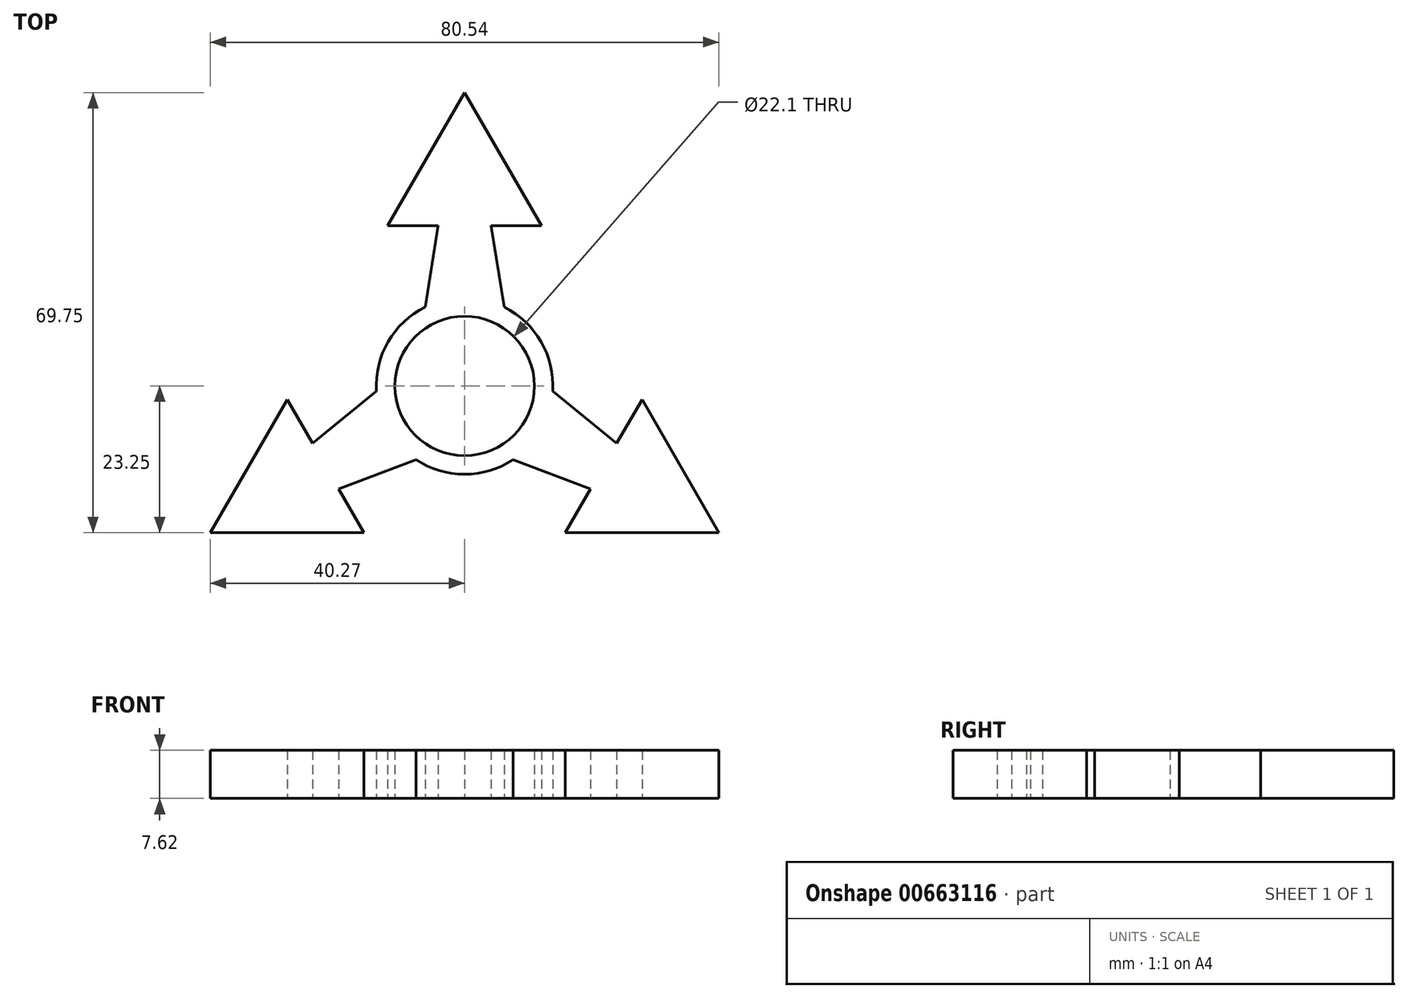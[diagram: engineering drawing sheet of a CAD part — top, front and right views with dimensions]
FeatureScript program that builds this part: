
annotation { "Feature Type Name" : "Feature", "Feature Type Description" : "" }
export const myFeature = defineFeature(function(context is Context, id is Id, definition is map)
    precondition{}
    {
        {
            var Q0;
            Q0=qCreatedBy(makeId("Top.planeOp"),FACE);
            var sketch = newSketch(context, id + "F0", { "sketchPlane" : qUnion([Q0])});
            skCircle(sketch, "E0", {"center": v(0, 0) * mm, "radius": 11.05 * mm});
            skArc(sketch, "E1", {"start": v(-6.26, 12.5) * mm, "mid": v(-12.11, 7) * mm, "end": v(-13.96, -0.84) * mm});
            skLineSegment(sketch, "E2.0", {"start": v(12.17, 25.41) * mm, "end": v(4.16, 25.41) * mm});
            skLineSegment(sketch, "E2.1", {"start": v(-12.17, 25.41) * mm, "end": v(0, 46.5) * mm});
            skLineSegment(sketch, "E2.2", {"start": v(0, 46.5) * mm, "end": v(12.17, 25.41) * mm});
            skPoint(sketch, "E2.0.midPoint", {"position": v(0, 25.41) * mm});
            skLineSegment(sketch, "E3", {"start": v(-4.17, 25.41) * mm, "end": v(-6.26, 12.5) * mm});
            skLineSegment(sketch, "E4", {"start": v(6.26, 12.5) * mm, "end": v(4.16, 25.41) * mm});
            skLineSegment(sketch, "E5.trimOffspring", {"start": v(-4.17, 25.41) * mm, "end": v(-12.17, 25.41) * mm});
            skPoint(sketch, "E2.cCircle.center.orphan", {"position": v(0, 32.44) * mm});
            skLineSegment(sketch, "E6.1.0", {"start": v(-13.96, -0.84) * mm, "end": v(-24.09, -9.1) * mm});
            skLineSegment(sketch, "E6.1.1", {"start": v(-28.1, -2.16) * mm, "end": v(-24.09, -9.1) * mm});
            skLineSegment(sketch, "E6.1.2", {"start": v(-40.27, -23.25) * mm, "end": v(-28.1, -2.16) * mm});
            skLineSegment(sketch, "E6.1.3", {"start": v(-15.92, -23.25) * mm, "end": v(-40.27, -23.25) * mm});
            skLineSegment(sketch, "E6.1.4", {"start": v(-19.93, -16.31) * mm, "end": v(-15.92, -23.25) * mm});
            skLineSegment(sketch, "E6.1.5", {"start": v(-19.93, -16.31) * mm, "end": v(-7.7, -11.67) * mm});
            skLineSegment(sketch, "E6.2.0", {"start": v(7.7, -11.67) * mm, "end": v(19.93, -16.31) * mm});
            skLineSegment(sketch, "E6.2.1", {"start": v(15.92, -23.25) * mm, "end": v(19.93, -16.31) * mm});
            skLineSegment(sketch, "E6.2.2", {"start": v(40.27, -23.25) * mm, "end": v(15.92, -23.25) * mm});
            skLineSegment(sketch, "E6.2.3", {"start": v(28.1, -2.16) * mm, "end": v(40.27, -23.25) * mm});
            skLineSegment(sketch, "E6.2.4", {"start": v(24.1, -9.1) * mm, "end": v(28.1, -2.16) * mm});
            skLineSegment(sketch, "E6.2.5", {"start": v(24.1, -9.1) * mm, "end": v(13.96, -0.84) * mm});
            skArc(sketch, "E7.trimOffspring", {"start": v(-7.7, -11.67) * mm, "mid": v(0, -13.98) * mm, "end": v(7.7, -11.67) * mm});
            skArc(sketch, "E8.trimOffspring", {"start": v(13.96, -0.84) * mm, "mid": v(12.11, 7) * mm, "end": v(6.26, 12.5) * mm});
            skSolve(sketch);
        }
        {
            var Q0;
            Q0 = qSketchRegion(id + "F0", true);
            extrude(context, id + "F1", {"entities" : qUnion([Q0]), "depth" : 7.62 * mm, "offsetDistance" : 25.4 * mm});
        }
    });
